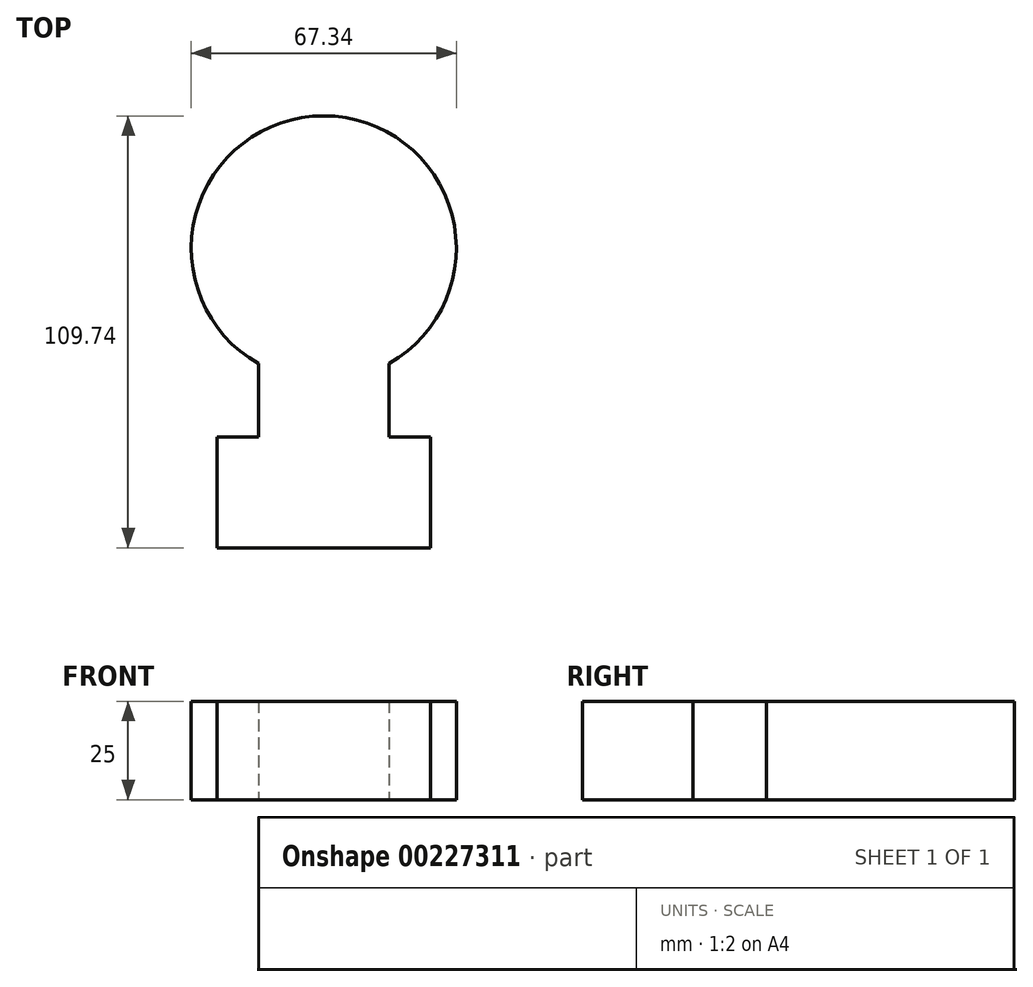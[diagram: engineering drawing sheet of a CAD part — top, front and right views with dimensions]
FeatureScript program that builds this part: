
annotation { "Feature Type Name" : "Feature", "Feature Type Description" : "" }
export const myFeature = defineFeature(function(context is Context, id is Id, definition is map)
    precondition{}
    {
        {
            var Q0;
            Q0=qCreatedBy(makeId("Top.planeOp"),FACE);
            var sketch = newSketch(context, id + "F0", { "sketchPlane" : qUnion([Q0])});
            skLineSegment(sketch, "E0.bottom", {"start": v(-16.62, 46.02) * mm, "end": v(16.62, 46.02) * mm});
            skLineSegment(sketch, "E0.top", {"start": v(-16.62, -46.02) * mm, "end": v(16.62, -46.02) * mm});
            skLineSegment(sketch, "E0.left", {"start": v(-16.62, 46.02) * mm, "end": v(-16.62, -46.02) * mm});
            skLineSegment(sketch, "E0.right", {"start": v(16.62, 46.02) * mm, "end": v(16.62, -46.02) * mm});
            skPoint(sketch, "E0.middle", {"position": v(0, 0) * mm});
            skSolve(sketch);
        }
        {
            var Q0;
            Q0=qCreatedBy(makeId("Top.planeOp"),FACE);
            var sketch = newSketch(context, id + "F1", { "sketchPlane" : qUnion([Q0])});
            skLineSegment(sketch, "E1", {"start": v(0, 0) * mm, "end": v(0, 46.28) * mm});
            skLineSegment(sketch, "E2", {"start": v(0, 46.28) * mm, "end": v(0, 23.14) * mm});
            skCircle(sketch, "E3", {"center": v(0, 23.14) * mm, "radius": 33.67 * mm});
            skSolve(sketch);
        }
        {
            var Q0;
            Q0=qCreatedBy(makeId("Top.planeOp"),FACE);
            var sketch = newSketch(context, id + "F2", { "sketchPlane" : qUnion([Q0])});
            skLineSegment(sketch, "E4.bottom", {"start": v(-27.1, -24.8) * mm, "end": v(27.1, -24.8) * mm});
            skLineSegment(sketch, "E4.top", {"start": v(-27.1, -52.93) * mm, "end": v(27.1, -52.93) * mm});
            skLineSegment(sketch, "E4.left", {"start": v(-27.1, -24.8) * mm, "end": v(-27.1, -52.93) * mm});
            skLineSegment(sketch, "E4.right", {"start": v(27.1, -24.8) * mm, "end": v(27.1, -52.93) * mm});
            skPoint(sketch, "E4.middle", {"position": v(0, -38.86) * mm});
            skSolve(sketch);
        }
        {
            var Q0;
            Q0=makeQuery(id+"F1.imprint","IMPRINT",FACE,{"disambiguationData":[TD([[makeQuery(id+"F1.imprint","IMPRINT",EDGE,{"derivedFrom":sQuery(id+"F1.wireOp",EDGE,"E3")}),1.0]])]});
            extrude(context, id + "F3", {"entities" : qUnion([Q0]), "depth" : 25 * mm});
        }
        {
            var Q0;
            Q0=makeQuery(id+"F0.imprint","IMPRINT",FACE,{"disambiguationData":[TD([[makeQuery(id+"F0.imprint","IMPRINT",EDGE,{"derivedFrom":sQuery(id+"F0.wireOp",EDGE,"E0.bottom")}),-1.0]])]});
            extrude(context, id + "F4", {"entities" : qUnion([Q0]), "operationType" : NewBodyOperationType.ADD, "depth" : 25 * mm});
        }
        {
            var Q0;
            Q0=makeQuery(id+"F2.imprint","IMPRINT",FACE,{"disambiguationData":[TD([[makeQuery(id+"F2.imprint","IMPRINT",EDGE,{"derivedFrom":sQuery(id+"F2.wireOp",EDGE,"E4.bottom")}),-1.0]])]});
            extrude(context, id + "F5", {"entities" : qUnion([Q0]), "operationType" : NewBodyOperationType.ADD, "depth" : 25 * mm});
        }
    });
